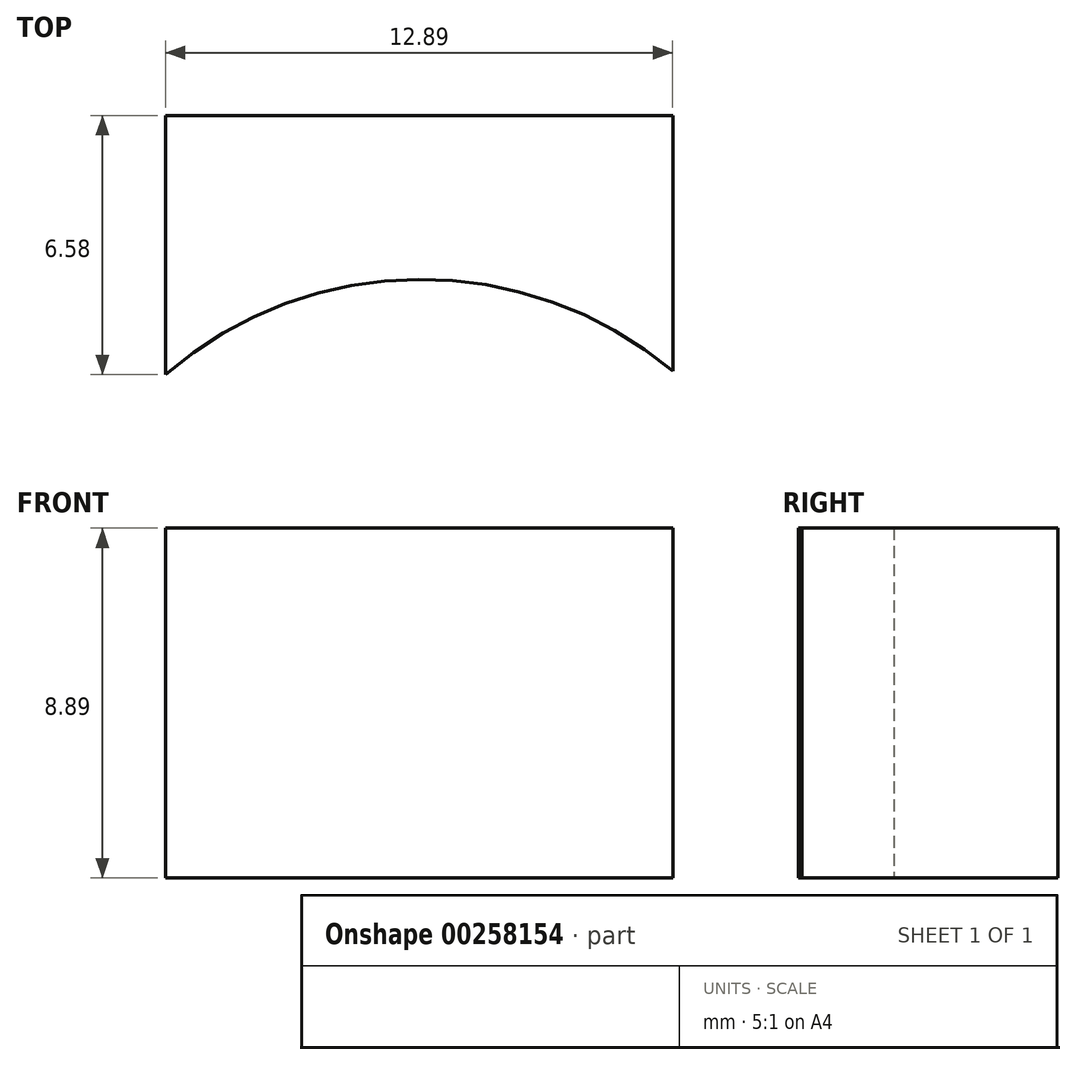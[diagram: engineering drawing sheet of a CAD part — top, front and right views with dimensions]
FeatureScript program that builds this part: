
annotation { "Feature Type Name" : "Feature", "Feature Type Description" : "" }
export const myFeature = defineFeature(function(context is Context, id is Id, definition is map)
    precondition{}
    {
        {
            var Q0;
            Q0=qCreatedBy(makeId("Top.planeOp"),FACE);
            var sketch = newSketch(context, id + "F0", { "sketchPlane" : qUnion([Q0])});
            skArc(sketch, "E0", {"start": v(6.4, 7.69) * mm, "mid": v(-0.07, 10.02) * mm, "end": v(-6.5, 7.6) * mm});
            skLineSegment(sketch, "E1", {"start": v(-6.5, 7.6) * mm, "end": v(-6.5, 14.18) * mm});
            skLineSegment(sketch, "E2", {"start": v(-6.5, 14.18) * mm, "end": v(6.4, 14.18) * mm});
            skLineSegment(sketch, "E3", {"start": v(6.4, 14.18) * mm, "end": v(6.4, 7.69) * mm});
            skSolve(sketch);
        }
        {
            var Q0;
            Q0=makeQuery(id+"F0.imprint","IMPRINT",FACE,{"disambiguationData":[TD([[makeQuery(id+"F0.imprint","IMPRINT",EDGE,{"derivedFrom":sQuery(id+"F0.wireOp",EDGE,"E0")}),-1.0]])]});
            extrude(context, id + "F1", {"entities" : qUnion([Q0]), "depth" : 8.9 * mm});
        }
    });
